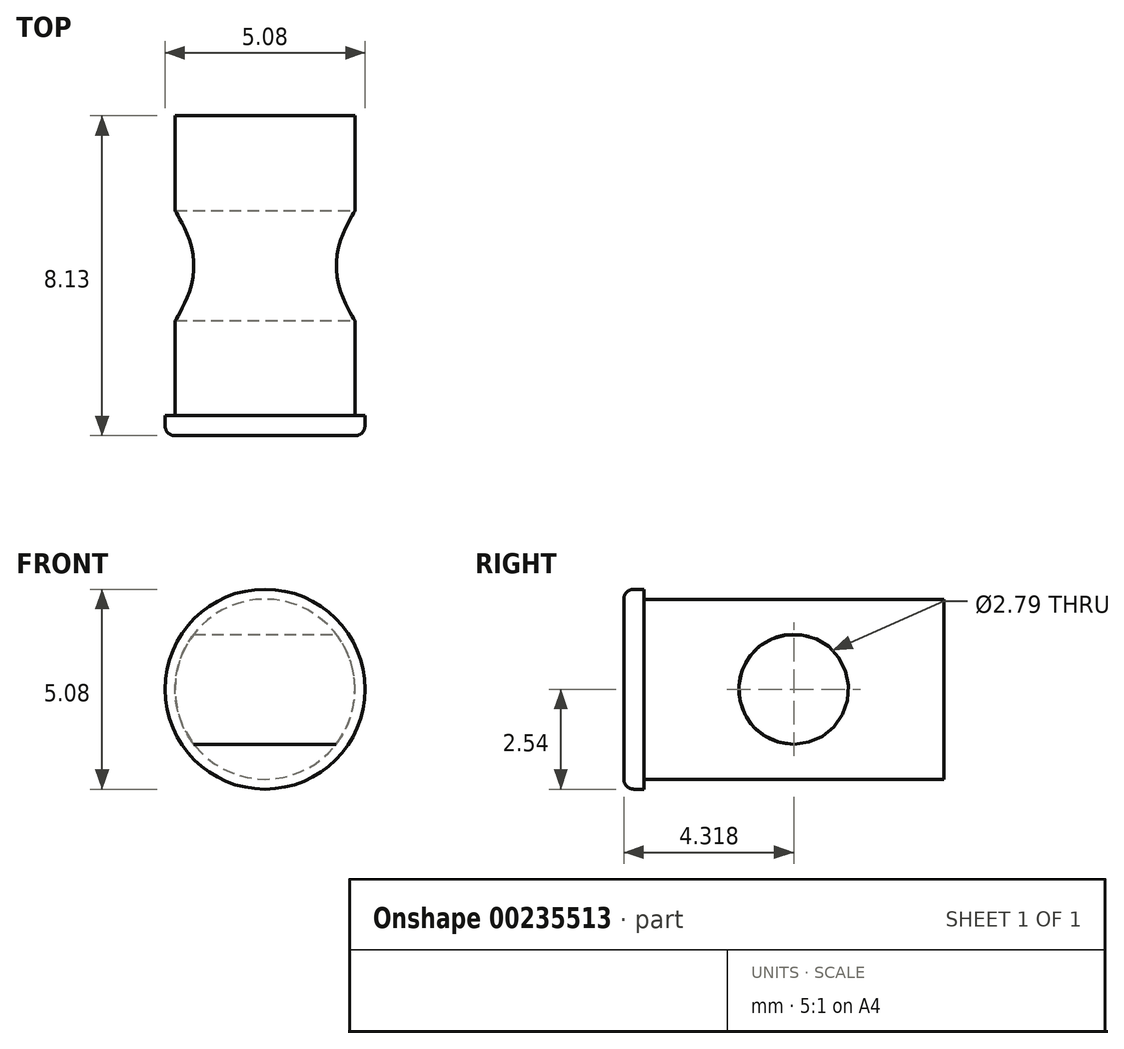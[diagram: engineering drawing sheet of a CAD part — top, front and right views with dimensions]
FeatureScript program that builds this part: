
annotation { "Feature Type Name" : "Feature", "Feature Type Description" : "" }
export const myFeature = defineFeature(function(context is Context, id is Id, definition is map)
    precondition{}
    {
        {
            var Q0;
            Q0=qCreatedBy(makeId("Front.planeOp"),FACE);
            var sketch = newSketch(context, id + "F0", { "sketchPlane" : qUnion([Q0])});
            skCircle(sketch, "E0", {"center": v(0, 0) * mm, "radius": 2.54 * mm});
            skCircle(sketch, "E1", {"center": v(0, 0) * mm, "radius": 2.29 * mm});
            skSolve(sketch);
        }
        {
            var Q0;
            Q0=makeQuery(id+"F0.imprint","IMPRINT",FACE,{"disambiguationData":[TD([[makeQuery(id+"F0.imprint","IMPRINT",EDGE,{"derivedFrom":sQuery(id+"F0.wireOp",EDGE,"E1")}),1.0]])]});
            extrude(context, id + "F1", {"entities" : qUnion([Q0]), "oppositeDirection" : true, "depth" : 8.13 * mm});
        }
        {
            var Q0;
            Q0=makeQuery(id+"F0.imprint","IMPRINT",FACE,{"disambiguationData":[TD([[makeQuery(id+"F0.imprint","IMPRINT",EDGE,{"derivedFrom":sQuery(id+"F0.wireOp",EDGE,"E0")}),1.0]])]});
            extrude(context, id + "F2", {"entities" : qUnion([Q0]), "operationType" : NewBodyOperationType.ADD, "oppositeDirection" : true, "depth" : 0.5 * mm});
        }
        {
            var Q0;
            Q0=qCreatedBy(makeId("Right.planeOp"),FACE);
            var sketch = newSketch(context, id + "F3", { "sketchPlane" : qUnion([Q0])});
            skCircle(sketch, "E2", {"center": v(4.32, 0) * mm, "radius": 1.4 * mm});
            skSolve(sketch);
        }
        {
            var Q0;
            Q0 = qSketchRegion(id + "F3", true);
            var Q1;
            Q1=makeQuery(id+"F1.opExtrude","SWEPT_FACE",FACE,{"disambiguationData":[OSD([sQuery(id+"F0.wireOp",EDGE,"E1")])]});
            extrude(context, id + "F4", {"entities" : qUnion([Q0]), "operationType" : NewBodyOperationType.REMOVE, "endBound" : BoundingType.SYMMETRIC, "oppositeDirection" : true, "endBoundEntityFace" : qUnion([Q1]), "depth" : 25.4 * mm});
        }
        {
            var Q0;
            Q0=makeQuery(id+"F2.opExtrude","CAP_EDGE",EDGE,{"disambiguationData":[OSD([sQuery(id+"F0.wireOp",EDGE,"E0")])],"isStart":true});
            fillet(context, id + "F5", {"entities" : qUnion([Q0]), "radius" : 0.25 * mm, "tangentPropagation" : true, "allowEdgeOverflow" : false});
        }
    });
